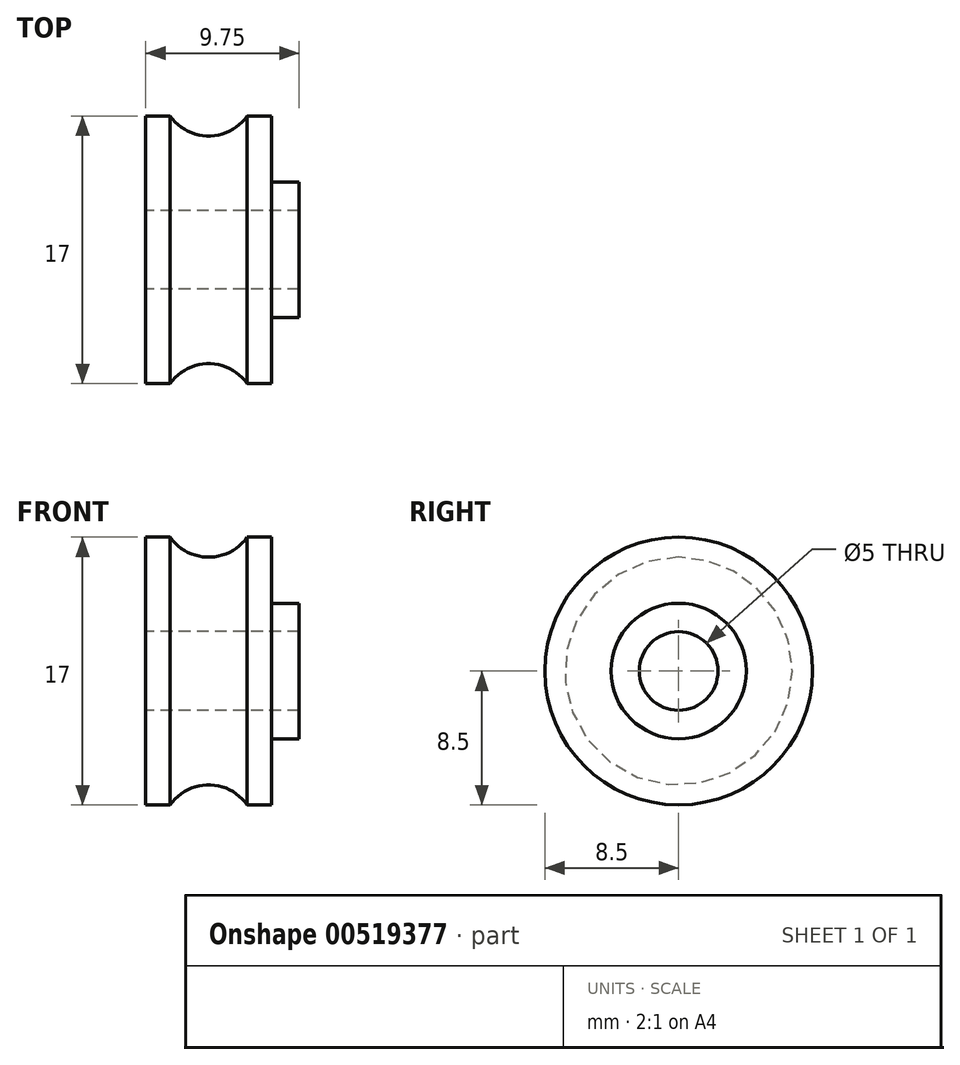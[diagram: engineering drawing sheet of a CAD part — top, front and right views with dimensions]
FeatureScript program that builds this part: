
annotation { "Feature Type Name" : "Feature", "Feature Type Description" : "" }
export const myFeature = defineFeature(function(context is Context, id is Id, definition is map)
    precondition{}
    {
        {
            var Q0;
            Q0=qCreatedBy(makeId("Top.planeOp"),FACE);
            var sketch = newSketch(context, id + "F0", { "sketchPlane" : qUnion([Q0])});
            skLineSegment(sketch, "E0", {"start": v(0, 0) * mm, "end": v(0, 6) * mm});
            skLineSegment(sketch, "E1", {"start": v(0, 6) * mm, "end": v(9.75, 6) * mm});
            skLineSegment(sketch, "E2", {"start": v(9.75, 6) * mm, "end": v(9.75, 4.2) * mm});
            skLineSegment(sketch, "E3", {"start": v(9.75, 4.2) * mm, "end": v(8, 4.2) * mm});
            skLineSegment(sketch, "E4", {"start": v(8, 4.2) * mm, "end": v(8, 0) * mm});
            skArc(sketch, "E5", {"start": v(6.45, 0) * mm, "mid": v(4, 1.27) * mm, "end": v(1.55, 0) * mm});
            skLineSegment(sketch, "E6", {"start": v(0, 0) * mm, "end": v(1.55, 0) * mm});
            skLineSegment(sketch, "E7", {"start": v(8, 0) * mm, "end": v(6.45, 0) * mm});
            skSolve(sketch);
        }
        {
            var Q0;
            Q0=qCreatedBy(makeId("Top.planeOp"),FACE);
            var sketch = newSketch(context, id + "F1", { "sketchPlane" : qUnion([Q0])});
            skLineSegment(sketch, "E8", {"start": v(1.6, 8.5) * mm, "end": v(19.32, 8.5) * mm, "construction": true});
            skSolve(sketch);
        }
        {
            var Q0;
            Q0 = qSketchRegion(id + "F0", true);
            var Q1;
            Q1=sQuery(id+"F1.wireOp",EDGE,"E8");
            revolve(context, id + "F2", {"entities" : qUnion([Q0]), "axis" : qUnion([Q1]), "revolveType" : RevolveType.FULL});
        }
    });
